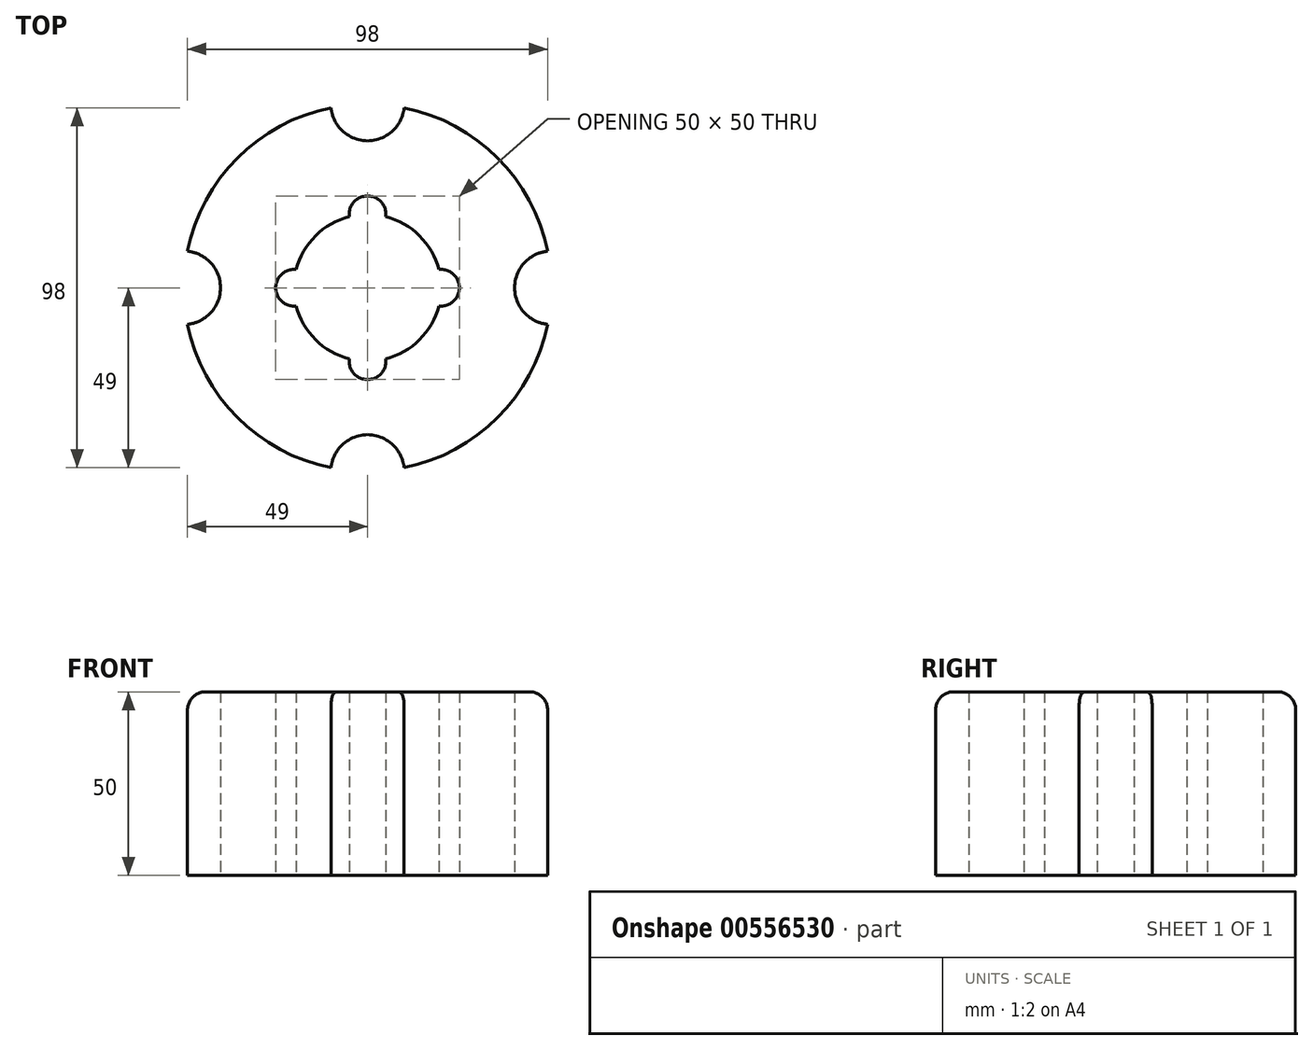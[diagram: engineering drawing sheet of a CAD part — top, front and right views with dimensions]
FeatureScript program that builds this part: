
annotation { "Feature Type Name" : "Feature", "Feature Type Description" : "" }
export const myFeature = defineFeature(function(context is Context, id is Id, definition is map)
    precondition{}
    {
        {
            var Q0;
            Q0=qCreatedBy(makeId("Top.planeOp"),FACE);
            var sketch = newSketch(context, id + "F0", { "sketchPlane" : qUnion([Q0])});
            skArc(sketch, "E0", {"start": v(-9.95, 49) * mm, "mid": v(-35.36, 35.36) * mm, "end": v(-49, 9.95) * mm});
            skArc(sketch, "E1", {"start": v(-9.95, 49) * mm, "mid": v(0, 40) * mm, "end": v(9.95, 49) * mm});
            skArc(sketch, "E2", {"start": v(-49, -9.95) * mm, "mid": v(-40, 0) * mm, "end": v(-49, 9.95) * mm});
            skArc(sketch, "E3", {"start": v(49, 9.95) * mm, "mid": v(40, 0) * mm, "end": v(49, -9.95) * mm});
            skArc(sketch, "E4", {"start": v(9.95, -49) * mm, "mid": v(0, -40) * mm, "end": v(-9.95, -49) * mm});
            skArc(sketch, "E5.trimOffspring", {"start": v(49, 9.95) * mm, "mid": v(35.36, 35.36) * mm, "end": v(9.95, 49) * mm});
            skArc(sketch, "E6.trimOffspring", {"start": v(9.95, -49) * mm, "mid": v(35.36, -35.36) * mm, "end": v(49, -9.95) * mm});
            skArc(sketch, "E7.trimOffspring", {"start": v(-49, -9.95) * mm, "mid": v(-35.36, -35.36) * mm, "end": v(-9.95, -49) * mm});
            skArc(sketch, "E8", {"start": v(-19.38, -4.96) * mm, "mid": v(-14.14, -14.14) * mm, "end": v(-4.96, -19.38) * mm});
            skArc(sketch, "E9", {"start": v(19.38, -4.96) * mm, "mid": v(25, 0) * mm, "end": v(19.38, 4.96) * mm});
            skArc(sketch, "E10", {"start": v(4.96, 19.38) * mm, "mid": v(0, 25) * mm, "end": v(-4.96, 19.38) * mm});
            skArc(sketch, "E11", {"start": v(-19.38, 4.96) * mm, "mid": v(-25, 0) * mm, "end": v(-19.37, -4.96) * mm});
            skArc(sketch, "E12", {"start": v(-4.96, -19.38) * mm, "mid": v(0, -25) * mm, "end": v(4.96, -19.38) * mm});
            skArc(sketch, "E13.trimOffspring", {"start": v(-4.96, 19.38) * mm, "mid": v(-14.14, 14.14) * mm, "end": v(-19.38, 4.96) * mm});
            skArc(sketch, "E14.trimOffspring", {"start": v(19.38, 4.96) * mm, "mid": v(14.14, 14.14) * mm, "end": v(4.96, 19.37) * mm});
            skArc(sketch, "E15.trimOffspring", {"start": v(4.96, -19.38) * mm, "mid": v(14.14, -14.14) * mm, "end": v(19.37, -4.96) * mm});
            skSolve(sketch);
        }
        {
            var Q0;
            Q0=makeQuery(id+"F0.imprint","IMPRINT",FACE,{"disambiguationData":[TD([[makeQuery(id+"F0.imprint","IMPRINT",EDGE,{"derivedFrom":sQuery(id+"F0.wireOp",EDGE,"E0")}),1.0]])]});
            extrude(context, id + "F1", {"entities" : qUnion([Q0]), "depth" : 50 * mm, "offsetDistance" : 25 * mm});
        }
        {
            var Q0;
            Q0=makeQuery(id+"F1.opExtrude","CAP_FACE",FACE,{"disambiguationData":[OSD([sQuery(id+"F0.wireOp",EDGE,"E0"),sQuery(id+"F0.wireOp",EDGE,"E1"),sQuery(id+"F0.wireOp",EDGE,"E2"),sQuery(id+"F0.wireOp",EDGE,"E3"),sQuery(id+"F0.wireOp",EDGE,"E4"),sQuery(id+"F0.wireOp",EDGE,"E5.trimOffspring"),sQuery(id+"F0.wireOp",EDGE,"E6.trimOffspring"),sQuery(id+"F0.wireOp",EDGE,"E7.trimOffspring"),sQuery(id+"F0.wireOp",EDGE,"E8"),sQuery(id+"F0.wireOp",EDGE,"E9"),sQuery(id+"F0.wireOp",EDGE,"E10"),sQuery(id+"F0.wireOp",EDGE,"E11"),sQuery(id+"F0.wireOp",EDGE,"E12"),sQuery(id+"F0.wireOp",EDGE,"E13.trimOffspring"),sQuery(id+"F0.wireOp",EDGE,"E14.trimOffspring"),sQuery(id+"F0.wireOp",EDGE,"E15.trimOffspring")])],"isStart":false});
            var sketch = newSketch(context, id + "F2", { "sketchPlane" : qUnion([Q0])});
            skSolve(sketch);
        }
        {
            var Q0;
            Q0=makeQuery(id+"F2.imprint","IMPRINT",FACE,{"disambiguationData":[TD([[makeQuery(id+"F2.imprint","IMPRINT",EDGE,{"derivedFrom":makeQuery(id+"F1.opExtrude","CAP_EDGE",EDGE,{"disambiguationData":[OSD([sQuery(id+"F0.wireOp",EDGE,"E0")])],"isStart":false})}),1.0]])]});
            var sketch = newSketch(context, id + "F3", { "sketchPlane" : qUnion([Q0])});
            skCircle(sketch, "E16", {"center": v(0, 32) * mm, "radius": 5 * mm});
            skCircle(sketch, "E17.1.0", {"center": v(27.71, 16) * mm, "radius": 5 * mm});
            skCircle(sketch, "E17.2.0", {"center": v(27.71, -16) * mm, "radius": 5 * mm});
            skCircle(sketch, "E17.3.0", {"center": v(0, -32) * mm, "radius": 5 * mm});
            skCircle(sketch, "E17.4.0", {"center": v(-27.71, -16) * mm, "radius": 5 * mm});
            skCircle(sketch, "E17.5.0", {"center": v(-27.71, 16) * mm, "radius": 5 * mm});
            skPoint(sketch, "E17.center", {"position": v(0, 0) * mm});
            skLineSegment(sketch, "E17.anchor1", {"start": v(0, 0) * mm, "end": v(0, 32) * mm, "construction": true});
            skLineSegment(sketch, "E17.anchor2", {"start": v(0, 0) * mm, "end": v(-27.71, 16) * mm, "construction": true});
            skSolve(sketch);
        }
        {
            var Q0;
            Q0=sQuery(id+"F3.wireOp",EDGE,"E17.2.0");
            var Q1;
            Q1=sQuery(id+"F3.wireOp",EDGE,"E17.1.0");
            var Q2;
            Q2=sQuery(id+"F3.wireOp",EDGE,"E16");
            var Q3;
            Q3=sQuery(id+"F3.wireOp",EDGE,"E17.5.0");
            var Q4;
            Q4=sQuery(id+"F3.wireOp",EDGE,"E17.4.0");
            var Q5;
            Q5=sQuery(id+"F3.wireOp",EDGE,"E17.3.0");
            extrude(context, id + "F4", {"bodyType" : ToolBodyType.SURFACE, "surfaceEntities" : qUnion([Q0, Q1, Q2, Q3, Q4, Q5]), "depth" : 50 * mm, "offsetDistance" : 25 * mm});
        }
        {
            var Q0;
            Q0=makeQuery(id+"F1.opExtrude","CAP_EDGE",EDGE,{"disambiguationData":[OSD([sQuery(id+"F0.wireOp",EDGE,"E6.trimOffspring")])],"isStart":false});
            var Q1;
            Q1=makeQuery(id+"F1.opExtrude","CAP_EDGE",EDGE,{"disambiguationData":[OSD([sQuery(id+"F0.wireOp",EDGE,"E5.trimOffspring")])],"isStart":false});
            var Q2;
            Q2=makeQuery(id+"F1.opExtrude","CAP_EDGE",EDGE,{"disambiguationData":[OSD([sQuery(id+"F0.wireOp",EDGE,"E7.trimOffspring")])],"isStart":false});
            var Q3;
            Q3=makeQuery(id+"F1.opExtrude","CAP_EDGE",EDGE,{"disambiguationData":[OSD([sQuery(id+"F0.wireOp",EDGE,"E0")])],"isStart":false});
            fillet(context, id + "F5", {"entities" : qUnion([Q0, Q1, Q2, Q3]), "radius" : 5 * mm, "tangentPropagation" : true, "allowEdgeOverflow" : false});
        }
    });
